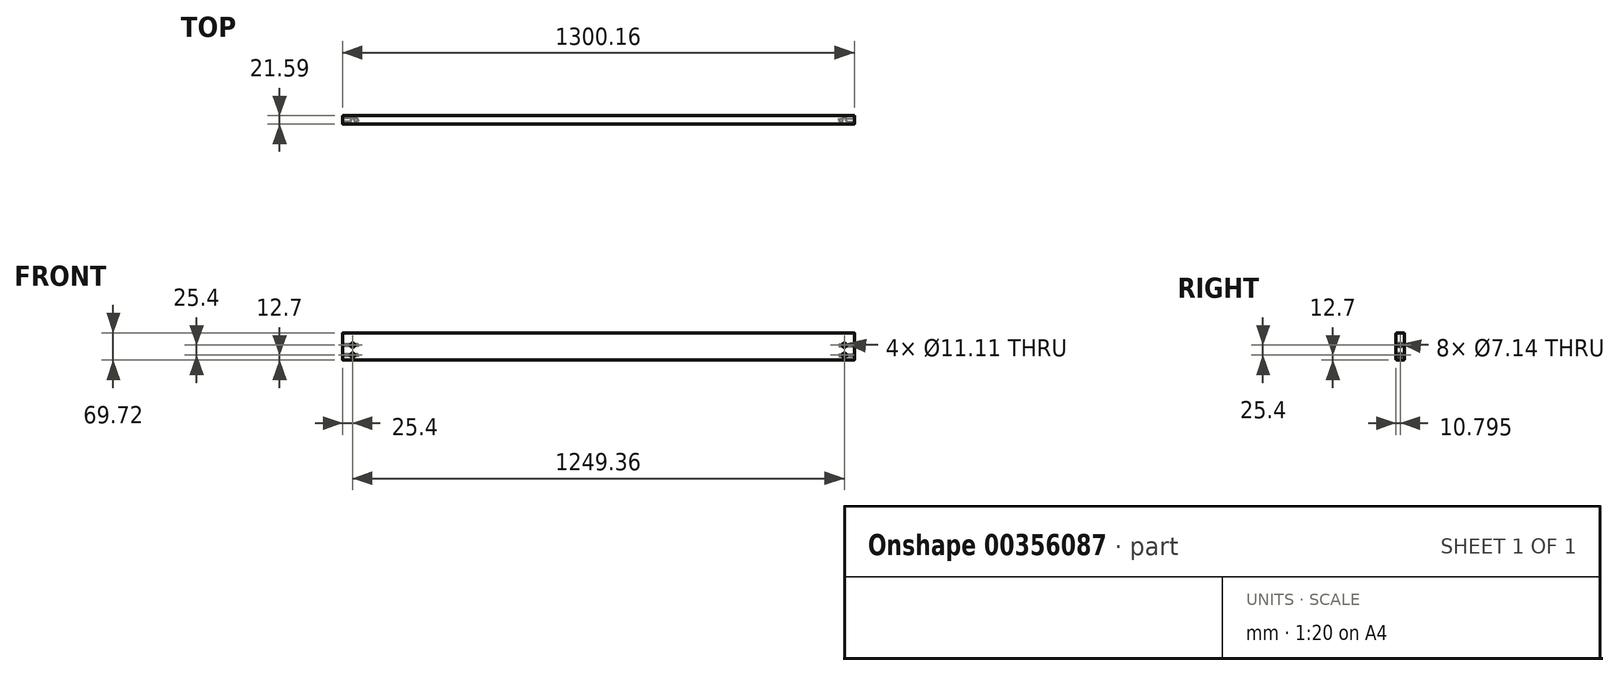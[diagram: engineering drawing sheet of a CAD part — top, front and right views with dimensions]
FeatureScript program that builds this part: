
annotation { "Feature Type Name" : "Feature", "Feature Type Description" : "" }
export const myFeature = defineFeature(function(context is Context, id is Id, definition is map)
    precondition{}
    {
        {
            var Q0;
            Q0=qCreatedBy(makeId("Right.planeOp"),FACE);
            var sketch = newSketch(context, id + "F0", { "sketchPlane" : qUnion([Q0])});
            skLineSegment(sketch, "E0.bottom", {"start": v(18.41, 0) * mm, "end": v(3.18, 0) * mm});
            skLineSegment(sketch, "E0.top", {"start": v(18.41, 69.72) * mm, "end": v(3.17, 69.72) * mm});
            skLineSegment(sketch, "E0.left", {"start": v(21.59, 3.18) * mm, "end": v(21.59, 66.55) * mm});
            skLineSegment(sketch, "E0.right", {"start": v(0, 3.17) * mm, "end": v(0, 66.55) * mm});
            skPoint(sketch, "E0.middle", {"position": v(0, 0) * mm});
            skPoint(sketch, "E1.visualSharp", {"position": v(0, 69.72) * mm});
            skArc(sketch, "E1.filletArc", {"start": v(3.17, 69.72) * mm, "mid": v(0.93, 68.8) * mm, "end": v(0, 66.55) * mm});
            skPoint(sketch, "E2.visualSharp", {"position": v(21.59, 69.72) * mm});
            skArc(sketch, "E2.filletArc", {"start": v(21.59, 66.55) * mm, "mid": v(20.66, 68.8) * mm, "end": v(18.41, 69.72) * mm});
            skPoint(sketch, "E3.visualSharp", {"position": v(21.59, 0) * mm});
            skArc(sketch, "E3.filletArc", {"start": v(18.41, 0) * mm, "mid": v(20.66, 0.93) * mm, "end": v(21.6, 3.18) * mm});
            skArc(sketch, "E4.filletArc", {"start": v(0, 3.17) * mm, "mid": v(0.93, 0.93) * mm, "end": v(3.18, 0) * mm});
            skSolve(sketch);
        }
        {
            var Q0;
            Q0=makeQuery(id+"F0.imprint","IMPRINT",FACE,{"disambiguationData":[TD([[makeQuery(id+"F0.imprint","IMPRINT",EDGE,{"derivedFrom":sQuery(id+"F0.wireOp",EDGE,"E0.bottom")}),-1.0]])]});
            extrude(context, id + "F1", {"entities" : qUnion([Q0]), "depth" : 1300.16 * mm});
        }
        {
            var Q0;
            Q0=makeQuery(id+"F1.opExtrude","CAP_FACE",FACE,{"disambiguationData":[OSD([sQuery(id+"F0.wireOp",EDGE,"E0.bottom"),sQuery(id+"F0.wireOp",EDGE,"E0.top"),sQuery(id+"F0.wireOp",EDGE,"E0.left"),sQuery(id+"F0.wireOp",EDGE,"E0.right"),sQuery(id+"F0.wireOp",EDGE,"E1.filletArc"),sQuery(id+"F0.wireOp",EDGE,"E2.filletArc"),sQuery(id+"F0.wireOp",EDGE,"E3.filletArc"),sQuery(id+"F0.wireOp",EDGE,"E4.filletArc")])],"isStart":true});
            var sketch = newSketch(context, id + "F2", { "sketchPlane" : qUnion([Q0])});
            skLineSegment(sketch, "E5", {"start": v(-10.8, 0) * mm, "end": v(-10.8, 69.72) * mm, "construction": true});
            skLineSegment(sketch, "E6", {"start": v(-21.59, 12.7) * mm, "end": v(0, 12.7) * mm, "construction": true});
            skLineSegment(sketch, "E7", {"start": v(-21.59, 38.1) * mm, "end": v(0, 38.1) * mm, "construction": true});
            skPoint(sketch, "E8", {"position": v(-10.8, 38.1) * mm});
            skPoint(sketch, "E9", {"position": v(-10.8, 12.7) * mm});
            skSolve(sketch);
        }
        {
            var Q0;
            Q0=makeQuery(id+"F1.opExtrude","CAP_FACE",FACE,{"disambiguationData":[OSD([sQuery(id+"F0.wireOp",EDGE,"E0.bottom"),sQuery(id+"F0.wireOp",EDGE,"E0.top"),sQuery(id+"F0.wireOp",EDGE,"E0.left"),sQuery(id+"F0.wireOp",EDGE,"E0.right"),sQuery(id+"F0.wireOp",EDGE,"E1.filletArc"),sQuery(id+"F0.wireOp",EDGE,"E2.filletArc"),sQuery(id+"F0.wireOp",EDGE,"E3.filletArc"),sQuery(id+"F0.wireOp",EDGE,"E4.filletArc")])],"isStart":false});
            var sketch = newSketch(context, id + "F3", { "sketchPlane" : qUnion([Q0])});
            skLineSegment(sketch, "E10.0", {"start": v(10.8, 0) * mm, "end": v(10.8, 69.72) * mm, "construction": true});
            skLineSegment(sketch, "E10.1", {"start": v(21.59, 12.7) * mm, "end": v(0, 12.7) * mm, "construction": true});
            skLineSegment(sketch, "E10.2", {"start": v(21.59, 38.1) * mm, "end": v(0, 38.1) * mm, "construction": true});
            skPoint(sketch, "E10.3", {"position": v(10.8, 38.1) * mm});
            skPoint(sketch, "E10.4", {"position": v(10.8, 12.7) * mm});
            skSolve(sketch);
        }
        {
            var Q0;
            Q0=sQuery(id+"F3.wireOp",VERTEX,"E10.3");
            var Q1;
            Q1=sQuery(id+"F3.wireOp",VERTEX,"E10.4");
            var Q2;
            Q2=sQuery(id+"F2.wireOp",VERTEX,"E8");
            var Q3;
            Q3=sQuery(id+"F2.wireOp",VERTEX,"E9");
            var Q4;
            Q4=makeQuery(id+"F1.opExtrude","SWEPT_BODY",BODY,{"disambiguationData":[OSD([sQuery(id+"F0.wireOp",EDGE,"E0.bottom"),sQuery(id+"F0.wireOp",EDGE,"E0.top"),sQuery(id+"F0.wireOp",EDGE,"E0.left"),sQuery(id+"F0.wireOp",EDGE,"E0.right"),sQuery(id+"F0.wireOp",EDGE,"E1.filletArc"),sQuery(id+"F0.wireOp",EDGE,"E2.filletArc"),sQuery(id+"F0.wireOp",EDGE,"E3.filletArc"),sQuery(id+"F0.wireOp",EDGE,"E4.filletArc")])]});
            hole(context, id + "F4", {"style" : HoleStyle.SIMPLE, "endStyle" : HoleEndStyle.BLIND, "holeDiameter" : 7.14 * mm, "holeDepth" : 38.1 * mm, "isTappedThrough" : true, "tappedDepth" : 12.7 * mm, "tapClearance" : 3, "locations" : qUnion([Q0, Q1, Q2, Q3]), "scope" : qUnion([Q4])});
        }
        {
            var Q0;
            Q0=makeQuery(id+"F1.opExtrude","SWEPT_FACE",FACE,{"disambiguationData":[OSD([sQuery(id+"F0.wireOp",EDGE,"E0.right")])]});
            var sketch = newSketch(context, id + "F5", { "sketchPlane" : qUnion([Q0])});
            skLineSegment(sketch, "E11.0", {"start": v(1300.16, 41.67) * mm, "end": v(1300.16, 34.53) * mm});
            skLineSegment(sketch, "E11.1", {"start": v(1300.16, 16.27) * mm, "end": v(1300.16, 9.13) * mm});
            skLineSegment(sketch, "E12", {"start": v(1300.16, 38.1) * mm, "end": v(1274.76, 38.1) * mm});
            skLineSegment(sketch, "E13", {"start": v(1300.16, 12.7) * mm, "end": v(1274.76, 12.7) * mm});
            skLineSegment(sketch, "E14", {"start": v(650.08, 3.17) * mm, "end": v(650.08, 66.55) * mm});
            skLineSegment(sketch, "E15.MirrorCS", {"start": v(0, 38.1) * mm, "end": v(25.4, 38.1) * mm});
            skLineSegment(sketch, "E16.MirrorCS", {"start": v(0, 12.7) * mm, "end": v(25.4, 12.7) * mm});
            skSolve(sketch);
        }
        {
            var Q0;
            Q0=sQuery(id+"F5.wireOp",VERTEX,"E15.MirrorCS.end");
            var Q1;
            Q1=sQuery(id+"F5.wireOp",VERTEX,"E16.MirrorCS.end");
            var Q2;
            Q2=sQuery(id+"F5.wireOp",VERTEX,"E12.end");
            var Q3;
            Q3=sQuery(id+"F5.wireOp",VERTEX,"E13.end");
            var Q4;
            Q4=makeQuery(id+"F1.opExtrude","SWEPT_BODY",BODY,{"disambiguationData":[OSD([sQuery(id+"F0.wireOp",EDGE,"E0.bottom"),sQuery(id+"F0.wireOp",EDGE,"E0.top"),sQuery(id+"F0.wireOp",EDGE,"E0.left"),sQuery(id+"F0.wireOp",EDGE,"E0.right"),sQuery(id+"F0.wireOp",EDGE,"E1.filletArc"),sQuery(id+"F0.wireOp",EDGE,"E2.filletArc"),sQuery(id+"F0.wireOp",EDGE,"E3.filletArc"),sQuery(id+"F0.wireOp",EDGE,"E4.filletArc")])]});
            hole(context, id + "F6", {"style" : HoleStyle.SIMPLE, "endStyle" : HoleEndStyle.BLIND, "holeDiameter" : 11.1 * mm, "holeDepth" : 15 * mm, "isTappedThrough" : true, "tappedDepth" : 12.7 * mm, "tapClearance" : 3, "locations" : qUnion([Q0, Q1, Q2, Q3]), "scope" : qUnion([Q4])});
        }
    });
